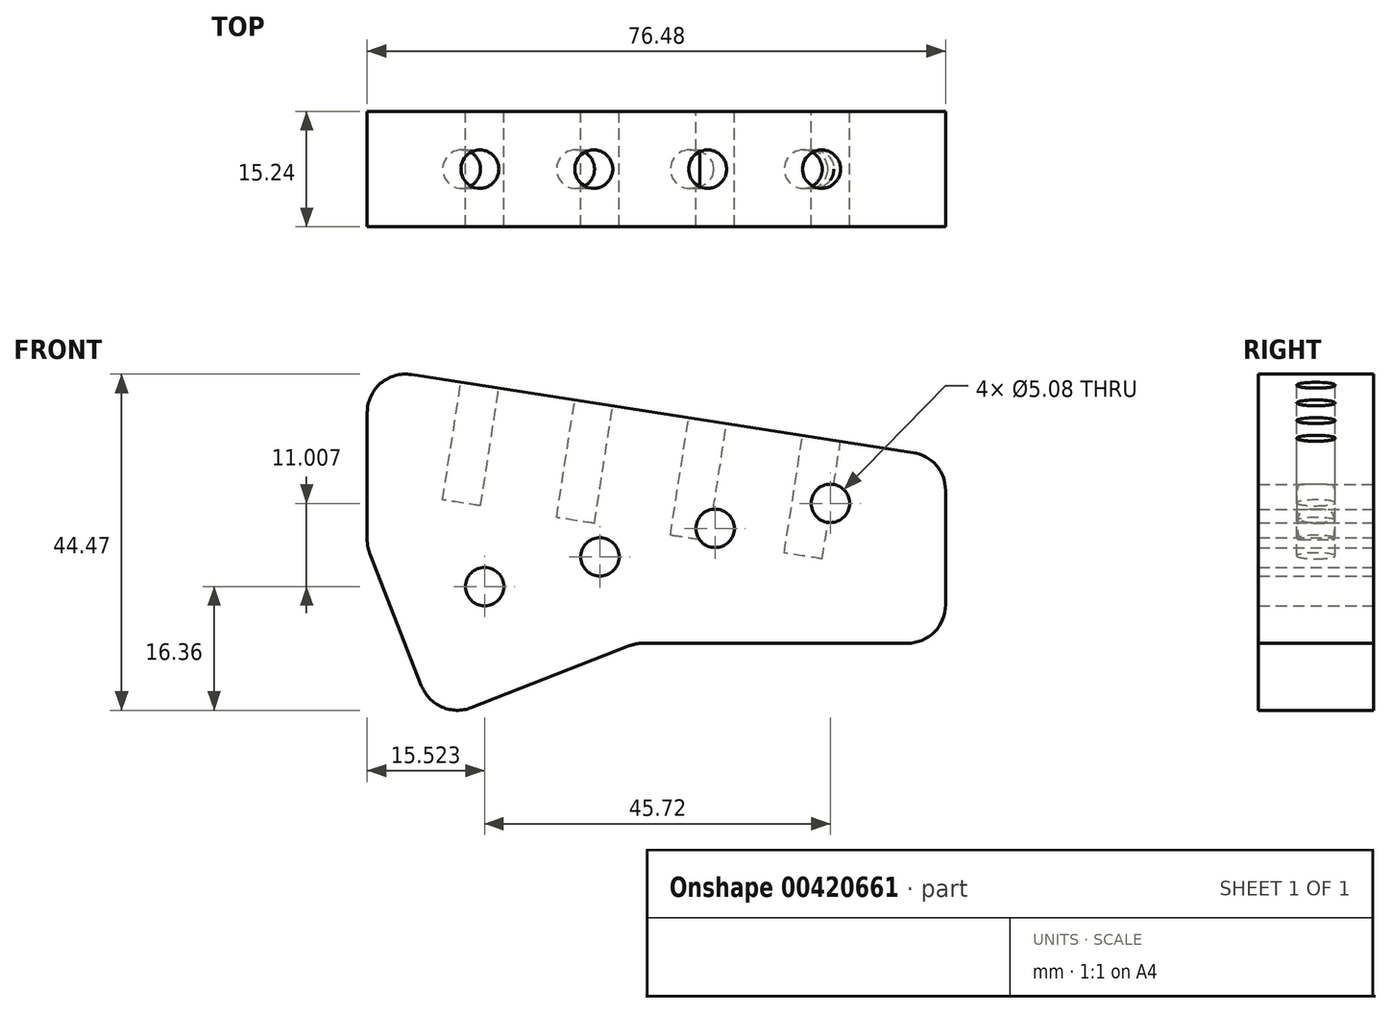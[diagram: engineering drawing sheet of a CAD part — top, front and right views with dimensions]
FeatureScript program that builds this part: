
annotation { "Feature Type Name" : "Feature", "Feature Type Description" : "" }
export const myFeature = defineFeature(function(context is Context, id is Id, definition is map)
    precondition{}
    {
        {
            var Q0;
            Q0=qCreatedBy(makeId("Front.planeOp"),FACE);
            var sketch = newSketch(context, id + "F0", { "sketchPlane" : qUnion([Q0])});
            skLineSegment(sketch, "E0", {"start": v(-26.82, -10.67) * mm, "end": v(-26.82, 12.85) * mm});
            skLineSegment(sketch, "E1", {"start": v(-26.82, 12.85) * mm, "end": v(49.66, 0.96) * mm});
            skLineSegment(sketch, "E2", {"start": v(49.66, 0.96) * mm, "end": v(49.66, -23.6) * mm});
            skLineSegment(sketch, "E3", {"start": v(49.66, -23.6) * mm, "end": v(8.71, -23.6) * mm});
            skLineSegment(sketch, "E4", {"start": v(8.71, -23.6) * mm, "end": v(-17.79, -33.98) * mm});
            skLineSegment(sketch, "E5", {"start": v(-17.79, -33.98) * mm, "end": v(-26.82, -10.9) * mm});
            skLineSegment(sketch, "E6", {"start": v(-26.82, -10.9) * mm, "end": v(-26.82, -10.67) * mm});
            skCircle(sketch, "E7", {"center": v(-11.3, -16.1) * mm, "radius": 2.54 * mm});
            skCircle(sketch, "E8", {"center": v(3.94, -12.18) * mm, "radius": 2.54 * mm});
            skCircle(sketch, "E9", {"center": v(19.18, -8.42) * mm, "radius": 2.54 * mm});
            skCircle(sketch, "E10", {"center": v(34.42, -5.1) * mm, "radius": 2.54 * mm});
            skSolve(sketch);
        }
        {
            var Q0;
            Q0=makeQuery(id+"F0.imprint","IMPRINT",FACE,{"disambiguationData":[TD([[makeQuery(id+"F0.imprint","IMPRINT",EDGE,{"derivedFrom":sQuery(id+"F0.wireOp",EDGE,"E0")}),-1.0]])]});
            extrude(context, id + "F1", {"entities" : qUnion([Q0]), "depth" : 15.24 * mm});
        }
        {
            var Q0;
            Q0=makeQuery(id+"F1.opExtrude","SWEPT_EDGE",EDGE,{"disambiguationData":[OSD([sQuery(id+"F0.wireOp",EDGE,"E0"),sQuery(id+"F0.wireOp",EDGE,"E1")])]});
            var Q1;
            Q1=makeQuery(id+"F1.opExtrude","SWEPT_EDGE",EDGE,{"disambiguationData":[OSD([sQuery(id+"F0.wireOp",EDGE,"E1"),sQuery(id+"F0.wireOp",EDGE,"E2")])]});
            var Q2;
            Q2=makeQuery(id+"F1.opExtrude","SWEPT_EDGE",EDGE,{"disambiguationData":[OSD([sQuery(id+"F0.wireOp",EDGE,"E2"),sQuery(id+"F0.wireOp",EDGE,"E3")])]});
            var Q3;
            Q3=makeQuery(id+"F1.opExtrude","SWEPT_EDGE",EDGE,{"disambiguationData":[OSD([sQuery(id+"F0.wireOp",EDGE,"E3"),sQuery(id+"F0.wireOp",EDGE,"E4")])]});
            var Q4;
            Q4=makeQuery(id+"F1.opExtrude","SWEPT_EDGE",EDGE,{"disambiguationData":[OSD([sQuery(id+"F0.wireOp",EDGE,"E4"),sQuery(id+"F0.wireOp",EDGE,"E5")])]});
            var Q5;
            Q5=makeQuery(id+"F1.opExtrude","SWEPT_EDGE",EDGE,{"disambiguationData":[OSD([sQuery(id+"F0.wireOp",EDGE,"E0"),sQuery(id+"F0.wireOp",EDGE,"E6")])]});
            fillet(context, id + "F2", {"entities" : qUnion([Q0, Q1, Q2, Q3, Q4, Q5]), "radius" : 5.08 * mm, "tangentPropagation" : true, "allowEdgeOverflow" : false});
        }
        {
            var Q0;
            Q0=makeQuery(id+"F1.opExtrude","SWEPT_FACE",FACE,{"disambiguationData":[OSD([sQuery(id+"F0.wireOp",EDGE,"E1")])]});
            var sketch = newSketch(context, id + "F3", { "sketchPlane" : qUnion([Q0])});
            skCircle(sketch, "E11", {"center": v(32.32, -7.62) * mm, "radius": 2.54 * mm});
            skCircle(sketch, "E12", {"center": v(17.08, -7.62) * mm, "radius": 2.54 * mm});
            skCircle(sketch, "E13", {"center": v(1.84, -7.62) * mm, "radius": 2.54 * mm});
            skCircle(sketch, "E14", {"center": v(-13.4, -7.62) * mm, "radius": 2.54 * mm});
            skLineSegment(sketch, "E15", {"start": v(43.28, -7.62) * mm, "end": v(-16.37, -7.62) * mm, "construction": true});
            skPoint(sketch, "E15.endSnap0", {"position": v(44.58, -7.62) * mm});
            skSolve(sketch);
        }
        {
            var Q0;
            Q0 = qSketchRegion(id + "F3", true);
            extrude(context, id + "F4", {"entities" : qUnion([Q0]), "operationType" : NewBodyOperationType.REMOVE, "oppositeDirection" : true, "depth" : 15.75 * mm});
        }
    });
